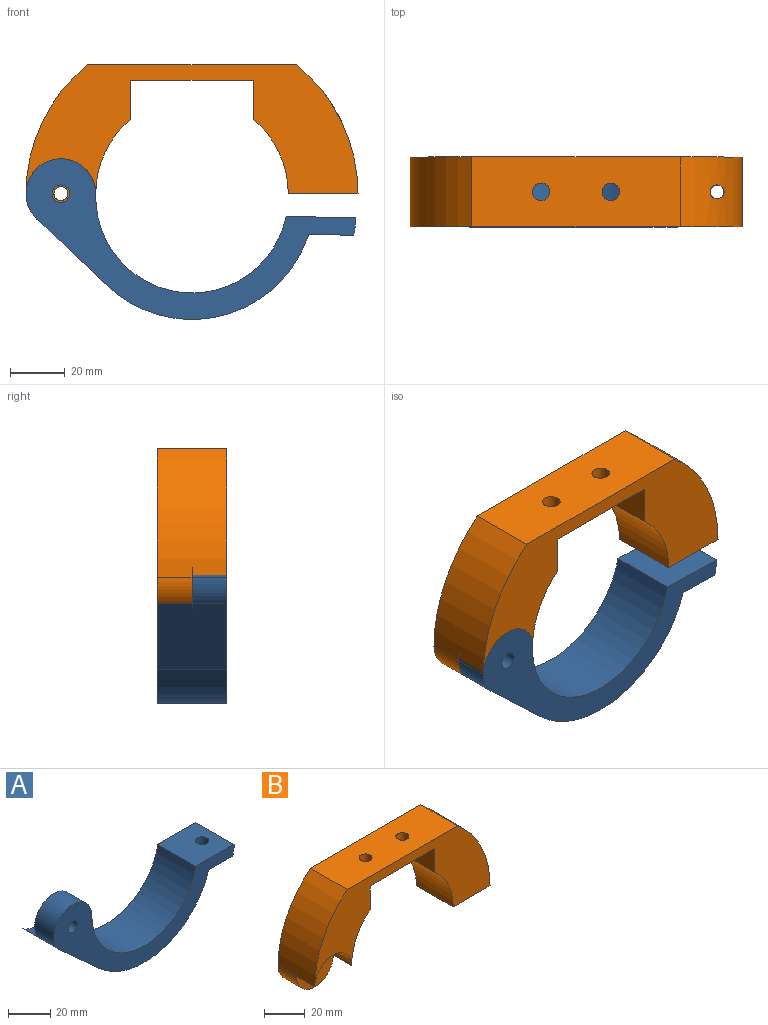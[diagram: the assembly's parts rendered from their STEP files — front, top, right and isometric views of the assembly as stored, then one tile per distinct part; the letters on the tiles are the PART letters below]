
ASSEMBLY  parts=2 mates=1
PART A: 14 faces, bbox 120.3x25.4x57.4 mm
  f0: plane 25.4x25.4mm, normal (0,1,0), area 475mm2, adj f1,f8,f11
  f1: cylinder r=12.7mm len=25.4mm, axis (0,1,0), area 641.6mm2, adj f0,f2,f9,f10
  f2: plane 26.3x25.4mm, normal (-0.67,0,-0.74), area 900.2mm2, adj f1,f3,f10,f11,f12
  f3: cylinder r=44.7mm len=72.82mm, axis (0,1,0), area 2290.5mm2, adj f2,f4,f10,f12
  f4: plane 25.4x16.24mm, normal (0,0,-1), area 380.8mm2, adj f3,f5,f10,f12,f13
  f5: cylinder r=60.45mm len=25.4mm, axis (0,1,0), area 112.1mm2, adj f4,f6,f10,f12
  f6: plane 25.4x2mm, normal (1,0,0), area 50.9mm2, adj f5,f7,f10,f12
  f7: plane 25.4x25.4mm, normal (0,0,1), area 613.5mm2, adj f6,f9,f10,f12,f13
  f8: cylinder r=3.17mm len=12.7mm, axis (0,1,0), area 253.4mm2, adj f0,f10
  f9: cylinder r=35.05mm len=69.52mm, axis (0,1,0), area 2634.8mm2, adj f1,f7,f10,f11,f12
  f10: plane 120.32x57.4mm, normal (0,-1,0), area 1719.9mm2, adj f1,f2,f3,f4,f5,f6,f7,f8
  f11: cylinder r=12.7mm len=21.21mm, axis (0,-1,0), area 371.8mm2, adj f0,f2,f9,f12
  f12: plane 116.14x44.7mm, normal (0,1,0), area 1244.8mm2, adj f2,f3,f4,f5,f6,f7,f9,f11
  f13: cylinder r=3.17mm len=6.35mm, axis (0,0,-1), area 126.7mm2, adj f4,f7
PART B: 18 faces, bbox 120.9x25.4x59.7 mm
  f0: cylinder r=12.7mm len=25.4mm, axis (0,1,0), area 506.7mm2, adj f1,f9,f10,f11
  f1: cylinder r=35.05mm len=27mm, axis (0,1,0), area 782.9mm2, adj f0,f2,f10,f12,f14
  f2: plane 25.4x14.32mm, normal (1,0,0), area 363.8mm2, adj f1,f3,f10,f14
  f3: plane 44.7x25.4mm, normal (0,0,-1), area 1072.1mm2, adj f2,f4,f10,f14,f16,f17
  f4: plane 25.4x14.32mm, normal (-1,0,0), area 363.8mm2, adj f3,f5,f10,f14
  f5: cylinder r=35.05mm len=27mm, axis (0,1,0), area 782.9mm2, adj f4,f6,f10,f14
  f6: plane 25.4x25.4mm, normal (0,0,-1), area 624.9mm2, adj f5,f7,f10,f14,f15
  f7: cylinder r=60.45mm len=46.98mm, axis (0,1,0), area 1328.1mm2, adj f6,f8,f10,f14,f15
  f8: plane 76.09x25.4mm, normal (0,0,1), area 1869.3mm2, adj f7,f9,f10,f14,f16,f17
  f9: cylinder r=60.45mm len=46.98mm, axis (0,1,0), area 1366.7mm2, adj f0,f8,f10,f12,f14
  f10: plane 120.9x46.98mm, normal (0,-1,0), area 2462.7mm2, adj f0,f1,f2,f3,f4,f5,f6,f7
  f11: plane 25.4x25.4mm, normal (0,-1,0), area 486.4mm2, adj f0,f12,f13
  f12: cylinder r=12.7mm len=25.4mm, axis (0,-1,0), area 506.7mm2, adj f1,f9,f11,f14
  f13: cylinder r=2.54mm len=12.7mm, axis (0,-1,0), area 202.7mm2, adj f11,f14
  f14: plane 120.9x59.68mm, normal (0,1,0), area 2949.1mm2, adj f1,f2,f3,f4,f5,f6,f7,f8
  f15: cylinder r=2.54mm len=35.64mm, axis (0,0,-1), area 505.7mm2, adj f6,f7
  f16: cylinder r=3.17mm len=6.35mm, axis (0,0,-1), area 112.9mm2, adj f3,f8
  f17: cylinder r=3.17mm len=6.35mm, axis (0,0,-1), area 112.9mm2, adj f3,f8
PLACE A rot(axis=(0,1,0),1.3deg) t=(-11.26,15.42,8.05)mm
PLACE B t=(-11.25,15.42,9.15)mm fixed
MATE revolute A.f1 <-> B.f0  axis (0,-1,0) through (-59,15.42,9.15)mm
